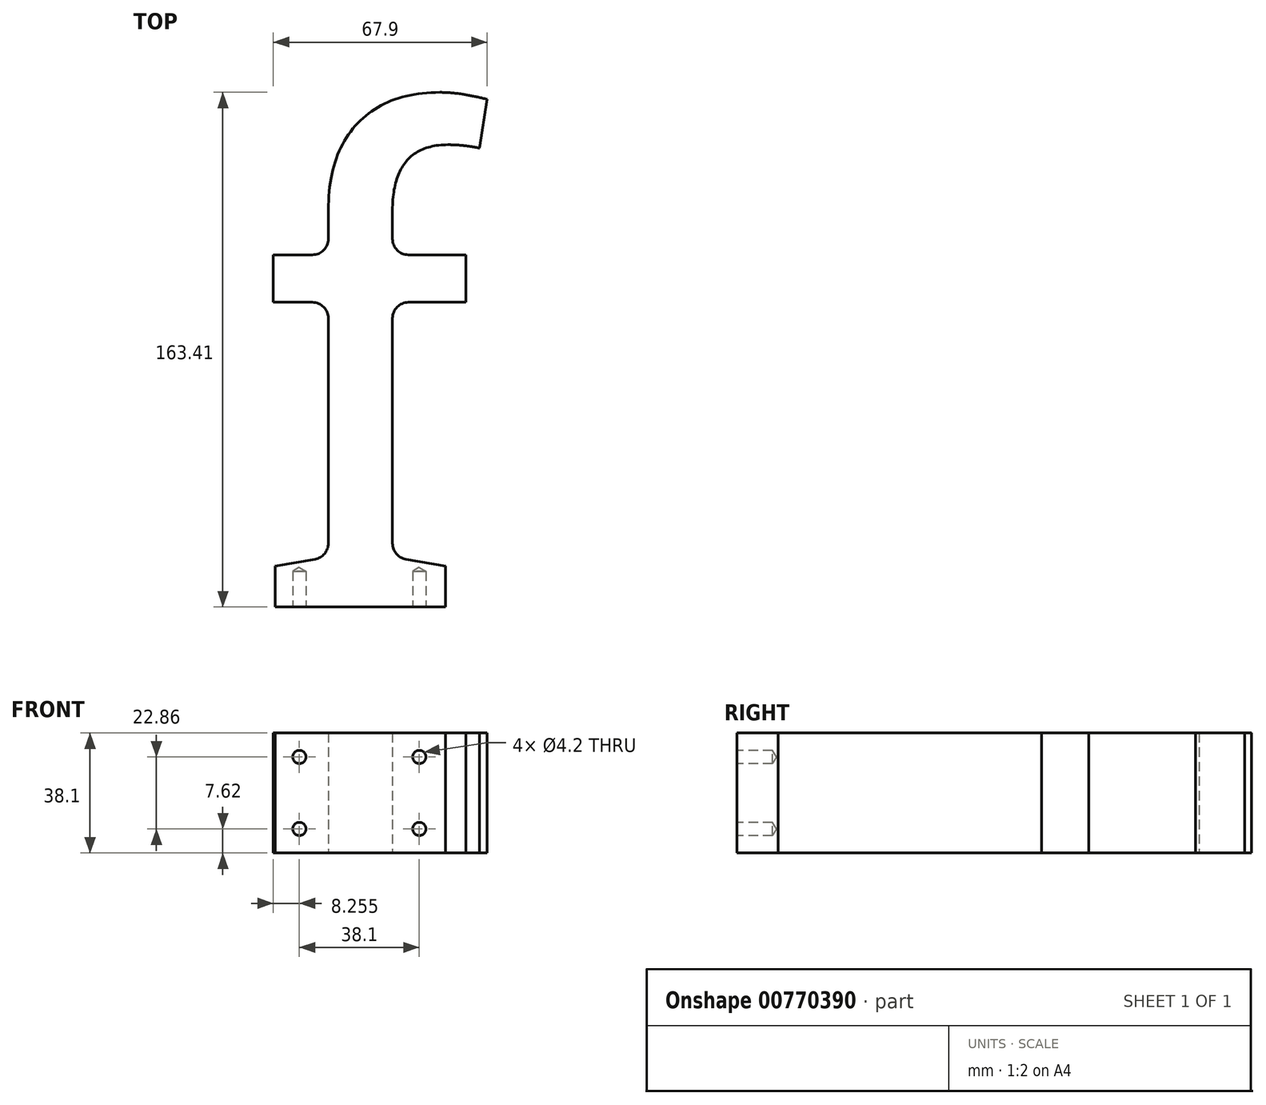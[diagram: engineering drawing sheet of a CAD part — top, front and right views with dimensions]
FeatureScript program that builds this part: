
annotation { "Feature Type Name" : "Feature", "Feature Type Description" : "" }
export const myFeature = defineFeature(function(context is Context, id is Id, definition is map)
    precondition{}
    {
        {
            var Q0;
            Q0=qCreatedBy(makeId("Top.planeOp"),FACE);
            var sketch = newSketch(context, id + "F0", { "sketchPlane" : qUnion([Q0])});
            skText(sketch, "E0", { "text": "f", "fontName": "RobotoSlab-Regular.ttf"});
            const initialGuessF0  = {"E0": [-0.04414, -0.06637, 1, 0, 0.1524]};
            skSetInitialGuess(sketch, initialGuessF0);
            skSolve(sketch);
        }
        {
            var Q0;
            Q0=makeQuery(id+"F0.imprint","IMPRINT",FACE,{"disambiguationData":[TD([[makeQuery(id+"F0.imprint","IMPRINT",EDGE,{"derivedFrom":sQuery(id+"F0.wireOp",EDGE,"E0.sketch_text.stroke-0")}),-1.0]])]});
            extrude(context, id + "F1", {"entities" : qUnion([Q0]), "depth" : 38.1 * mm, "offsetDistance" : 25 * mm});
        }
        {
            var Q0;
            Q0=makeQuery(id+"F1.opExtrude","SWEPT_EDGE",EDGE,{"disambiguationData":[OSD([sQuery(id+"F0.wireOp",EDGE,"E0.sketch_text.stroke-15"),sQuery(id+"F0.wireOp",EDGE,"E0.sketch_text.stroke-16")])]});
            var Q1;
            Q1=makeQuery(id+"F1.opExtrude","SWEPT_EDGE",EDGE,{"disambiguationData":[OSD([sQuery(id+"F0.wireOp",EDGE,"E0.sketch_text.stroke-22"),sQuery(id+"F0.wireOp",EDGE,"E0.sketch_text.stroke-23")])]});
            var Q2;
            Q2=makeQuery(id+"F1.opExtrude","SWEPT_EDGE",EDGE,{"disambiguationData":[OSD([sQuery(id+"F0.wireOp",EDGE,"E0.sketch_text.stroke-12"),sQuery(id+"F0.wireOp",EDGE,"E0.sketch_text.stroke-13")])]});
            var Q3;
            Q3=makeQuery(id+"F1.opExtrude","SWEPT_EDGE",EDGE,{"disambiguationData":[OSD([sQuery(id+"F0.wireOp",EDGE,"E0.sketch_text.stroke-1"),sQuery(id+"F0.wireOp",EDGE,"E0.sketch_text.stroke-2")])]});
            var Q4;
            Q4=makeQuery(id+"F1.opExtrude","SWEPT_EDGE",EDGE,{"disambiguationData":[OSD([sQuery(id+"F0.wireOp",EDGE,"E0.sketch_text.stroke-16"),sQuery(id+"F0.wireOp",EDGE,"E0.sketch_text.stroke-17")])]});
            var Q5;
            Q5=makeQuery(id+"F1.opExtrude","SWEPT_EDGE",EDGE,{"disambiguationData":[OSD([sQuery(id+"F0.wireOp",EDGE,"E0.sketch_text.stroke-21"),sQuery(id+"F0.wireOp",EDGE,"E0.sketch_text.stroke-22")])]});
            fillet(context, id + "F2", {"entities" : qUnion([Q0, Q1, Q2, Q3, Q4, Q5]), "radius" : 5.08 * mm, "tangentPropagation" : true, "allowEdgeOverflow" : false});
        }
        {
            var Q0;
            Q0=makeQuery(id+"F1.opExtrude","SWEPT_FACE",FACE,{"disambiguationData":[OSD([sQuery(id+"F0.wireOp",EDGE,"E0.sketch_text.stroke-19")])]});
            var sketch = newSketch(context, id + "F3", { "sketchPlane" : qUnion([Q0])});
            skLineSegment(sketch, "E1.bottom", {"start": v(-28.64, 30.48) * mm, "end": v(9.46, 30.48) * mm});
            skLineSegment(sketch, "E1.top", {"start": v(-28.64, 7.62) * mm, "end": v(9.46, 7.62) * mm});
            skLineSegment(sketch, "E1.left", {"start": v(-28.64, 30.48) * mm, "end": v(-28.64, 7.62) * mm});
            skLineSegment(sketch, "E1.right", {"start": v(9.46, 30.48) * mm, "end": v(9.46, 7.62) * mm});
            skSolve(sketch);
        }
        {
            var Q0;
            Q0=sQuery(id+"F3.wireOp",VERTEX,"E1.bottom.start");
            var Q1;
            Q1=sQuery(id+"F3.wireOp",VERTEX,"E1.bottom.end");
            var Q2;
            Q2=sQuery(id+"F3.wireOp",VERTEX,"E1.top.end");
            var Q3;
            Q3=sQuery(id+"F3.wireOp",VERTEX,"E1.top.start");
            var Q4;
            Q4=makeQuery(id+"F1.opExtrude","SWEPT_BODY",BODY,{"disambiguationData":[OSD([sQuery(id+"F0.wireOp",EDGE,"E0.sketch_text.stroke-0"),sQuery(id+"F0.wireOp",EDGE,"E0.sketch_text.stroke-1"),sQuery(id+"F0.wireOp",EDGE,"E0.sketch_text.stroke-2"),sQuery(id+"F0.wireOp",EDGE,"E0.sketch_text.stroke-3"),sQuery(id+"F0.wireOp",EDGE,"E0.sketch_text.stroke-4"),sQuery(id+"F0.wireOp",EDGE,"E0.sketch_text.stroke-5"),sQuery(id+"F0.wireOp",EDGE,"E0.sketch_text.stroke-6"),sQuery(id+"F0.wireOp",EDGE,"E0.sketch_text.stroke-7"),sQuery(id+"F0.wireOp",EDGE,"E0.sketch_text.stroke-8"),sQuery(id+"F0.wireOp",EDGE,"E0.sketch_text.stroke-9"),sQuery(id+"F0.wireOp",EDGE,"E0.sketch_text.stroke-10"),sQuery(id+"F0.wireOp",EDGE,"E0.sketch_text.stroke-11"),sQuery(id+"F0.wireOp",EDGE,"E0.sketch_text.stroke-12"),sQuery(id+"F0.wireOp",EDGE,"E0.sketch_text.stroke-13"),sQuery(id+"F0.wireOp",EDGE,"E0.sketch_text.stroke-14"),sQuery(id+"F0.wireOp",EDGE,"E0.sketch_text.stroke-15"),sQuery(id+"F0.wireOp",EDGE,"E0.sketch_text.stroke-16"),sQuery(id+"F0.wireOp",EDGE,"E0.sketch_text.stroke-17"),sQuery(id+"F0.wireOp",EDGE,"E0.sketch_text.stroke-18"),sQuery(id+"F0.wireOp",EDGE,"E0.sketch_text.stroke-19"),sQuery(id+"F0.wireOp",EDGE,"E0.sketch_text.stroke-20"),sQuery(id+"F0.wireOp",EDGE,"E0.sketch_text.stroke-21"),sQuery(id+"F0.wireOp",EDGE,"E0.sketch_text.stroke-22"),sQuery(id+"F0.wireOp",EDGE,"E0.sketch_text.stroke-23")])]});
            hole(context, id + "F4", {"style" : HoleStyle.SIMPLE, "endStyle" : HoleEndStyle.BLIND, "standardTappedOrClearance" : lookupTablePath({ "standard" : "ISO", "engagement" : "75%", "pitch" : "0.8 mm", "size" : "M5", "type" : "Tapped" }), "standardBlindInLast" : lookupTablePath({ "standard" : "ISO", "engagement" : "75%", "pitch" : "0.8 mm", "size" : "M5", "type" : "Tapped" }), "holeDiameter" : 4.2 * mm, "majorDiameter" : 5 * mm, "showTappedDepth" : true, "holeDepth" : 11.29 * mm, "tappedDepth" : 8.9 * mm, "tapClearance" : 3, "locations" : qUnion([Q0, Q1, Q2, Q3]), "scope" : qUnion([Q4])});
        }
    });
